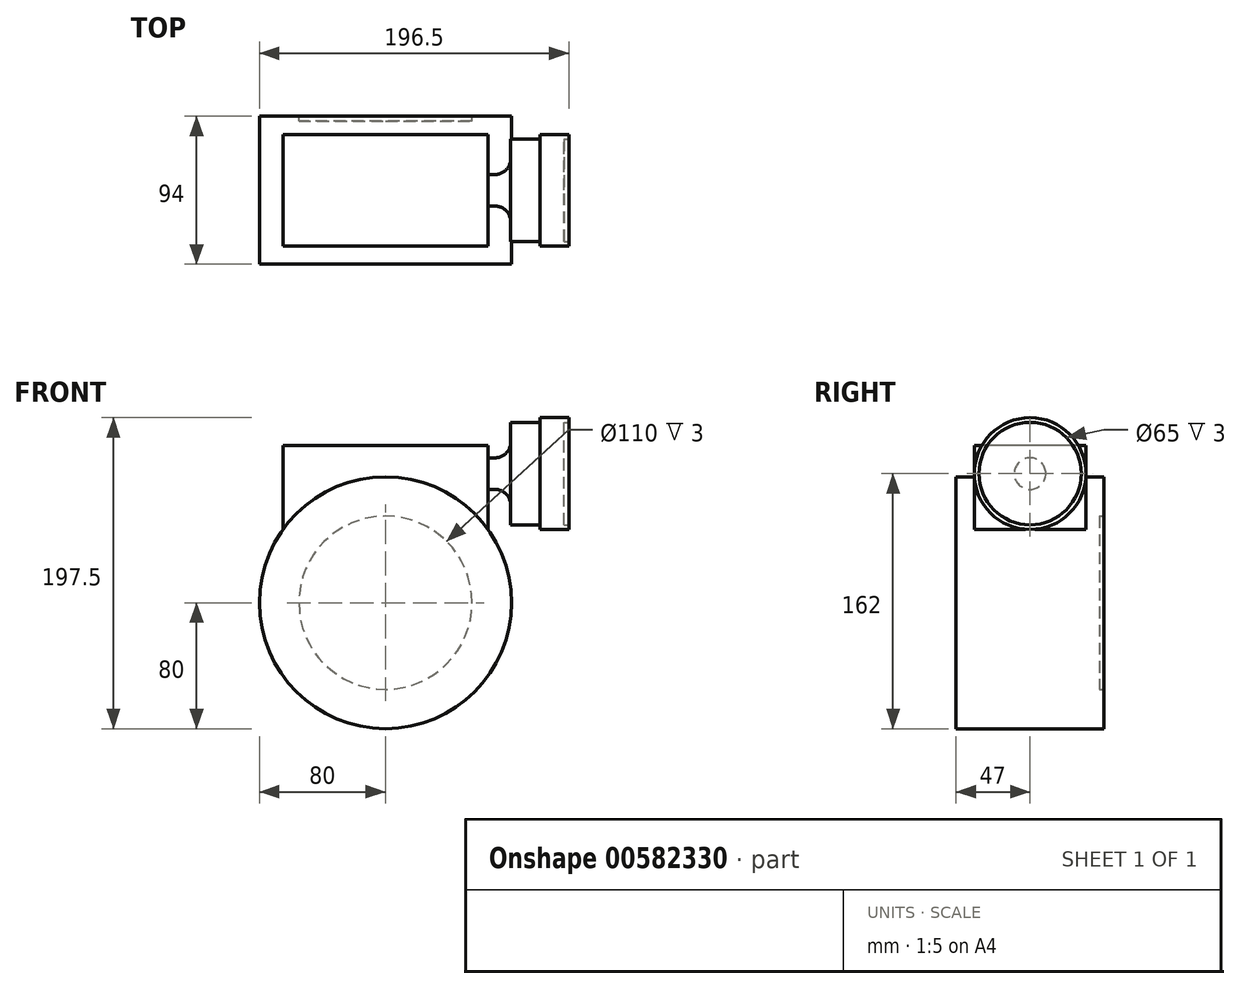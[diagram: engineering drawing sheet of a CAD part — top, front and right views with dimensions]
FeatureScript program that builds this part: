
annotation { "Feature Type Name" : "Feature", "Feature Type Description" : "" }
export const myFeature = defineFeature(function(context is Context, id is Id, definition is map)
    precondition{}
    {
        {
            var Q0;
            Q0=qCreatedBy(makeId("Front.planeOp"),FACE);
            var sketch = newSketch(context, id + "F0", { "sketchPlane" : qUnion([Q0])});
            skCircle(sketch, "E0", {"center": v(0, 0) * mm, "radius": 80 * mm});
            skSolve(sketch);
        }
        {
            var Q0;
            Q0=makeQuery(id+"F0.imprint","IMPRINT",FACE,{"disambiguationData":[TD([[makeQuery(id+"F0.imprint","IMPRINT",EDGE,{"derivedFrom":sQuery(id+"F0.wireOp",EDGE,"E0")}),1.0]])]});
            extrude(context, id + "F1", {"entities" : qUnion([Q0]), "depth" : 47 * mm, "offsetDistance" : 25 * mm});
        }
        {
            var Q0;
            Q0=qCreatedBy(makeId("Top.planeOp"),FACE);
            var sketch = newSketch(context, id + "F2", { "sketchPlane" : qUnion([Q0])});
            skLineSegment(sketch, "E1.bottom", {"start": v(-65, 35.5) * mm, "end": v(65, 35.5) * mm});
            skLineSegment(sketch, "E1.top", {"start": v(-65, -35.5) * mm, "end": v(65, -35.5) * mm});
            skLineSegment(sketch, "E1.left", {"start": v(-65, 35.5) * mm, "end": v(-65, -35.5) * mm});
            skLineSegment(sketch, "E1.right", {"start": v(65, 35.5) * mm, "end": v(65, -35.5) * mm});
            skPoint(sketch, "E1.middle", {"position": v(0, 0) * mm});
            skSolve(sketch);
        }
        {
            var Q0;
            Q0=makeQuery(id+"F2.imprint","IMPRINT",FACE,{"disambiguationData":[TD([[makeQuery(id+"F2.imprint","IMPRINT",EDGE,{"derivedFrom":sQuery(id+"F2.wireOp",EDGE,"E1.bottom")}),-1.0]])]});
            extrude(context, id + "F3", {"entities" : qUnion([Q0]), "operationType" : NewBodyOperationType.ADD, "depth" : 100 * mm, "offsetDistance" : 25 * mm});
        }
        {
            var Q0;
            Q0=qCreatedBy(makeId("Front.planeOp"),FACE);
            var sketch = newSketch(context, id + "F4", { "sketchPlane" : qUnion([Q0])});
            skLineSegment(sketch, "E2.bottom", {"start": v(0, 92) * mm, "end": v(79.5, 92) * mm});
            skLineSegment(sketch, "E2.top", {"start": v(0, 82) * mm, "end": v(79.5, 82) * mm});
            skLineSegment(sketch, "E2.left", {"start": v(0, 92) * mm, "end": v(0, 82) * mm});
            skLineSegment(sketch, "E2.right", {"start": v(79.5, 92) * mm, "end": v(79.5, 82) * mm});
            skPoint(sketch, "E2.middle", {"position": v(39.75, 87) * mm});
            skLineSegment(sketch, "E3", {"start": v(79.5, 92) * mm, "end": v(79.5, 114.5) * mm});
            skLineSegment(sketch, "E4", {"start": v(79.5, 114.5) * mm, "end": v(98, 114.5) * mm});
            skLineSegment(sketch, "E5", {"start": v(98, 114.5) * mm, "end": v(98, 117.5) * mm});
            skLineSegment(sketch, "E6", {"start": v(98, 117.5) * mm, "end": v(116.5, 117.5) * mm});
            skLineSegment(sketch, "E7", {"start": v(116.5, 117.5) * mm, "end": v(116.5, 114.5) * mm});
            skLineSegment(sketch, "E8", {"start": v(116.5, 114.5) * mm, "end": v(113.5, 114.5) * mm});
            skLineSegment(sketch, "E9", {"start": v(113.5, 114.5) * mm, "end": v(113.5, 82) * mm});
            skLineSegment(sketch, "E10", {"start": v(113.5, 82) * mm, "end": v(79.5, 82) * mm});
            skSolve(sketch);
        }
        {
            var Q0;
            Q0=makeQuery(id+"F4.imprint","IMPRINT",FACE,{"disambiguationData":[TD([[makeQuery(id+"F4.imprint","IMPRINT",EDGE,{"derivedFrom":sQuery(id+"F4.wireOp",EDGE,"E2.right")}),1.0]])]});
            var Q1;
            Q1=makeQuery(id+"F4.imprint","IMPRINT",FACE,{"disambiguationData":[TD([[makeQuery(id+"F4.imprint","IMPRINT",EDGE,{"derivedFrom":sQuery(id+"F4.wireOp",EDGE,"E2.bottom")}),-1.0]])]});
            var Q2;
            Q2=sQuery(id+"F4.wireOp",EDGE,"E10");
            revolve(context, id + "F5", {"operationType" : NewBodyOperationType.ADD, "entities" : qUnion([Q0, Q1]), "axis" : qUnion([Q2]), "revolveType" : RevolveType.FULL});
        }
        {
            var Q0;
            Q0=makeQuery(id+"F5.opRevolve","SWEPT_EDGE",EDGE,{"disambiguationData":[OSD([sQuery(id+"F4.wireOp",EDGE,"E2.bottom"),sQuery(id+"F4.wireOp",EDGE,"E2.right"),sQuery(id+"F4.wireOp",EDGE,"E3")])]});
            fillet(context, id + "F6", {"entities" : qUnion([Q0]), "radius" : 10 * mm, "tangentPropagation" : true, "allowEdgeOverflow" : false});
        }
        {
            var Q0;
            Q0=qCreatedBy(makeId("Front.planeOp"),FACE);
            var sketch = newSketch(context, id + "F7", { "sketchPlane" : qUnion([Q0])});
            skCircle(sketch, "E11", {"center": v(0, 0) * mm, "radius": 80 * mm});
            skSolve(sketch);
        }
        {
            var Q0;
            Q0=makeQuery(id+"F7.imprint","IMPRINT",FACE,{"disambiguationData":[TD([[makeQuery(id+"F7.imprint","IMPRINT",EDGE,{"derivedFrom":sQuery(id+"F7.wireOp",EDGE,"E11")}),1.0]])]});
            extrude(context, id + "F8", {"entities" : qUnion([Q0]), "operationType" : NewBodyOperationType.ADD, "oppositeDirection" : true, "depth" : (94 - 47) * mm, "offsetDistance" : 25 * mm});
        }
        {
            var Q0;
            Q0=makeQuery(id+"F8.opExtrude","CAP_FACE",FACE,{"disambiguationData":[OSD([sQuery(id+"F7.wireOp",EDGE,"E11")])],"isStart":false});
            var sketch = newSketch(context, id + "F9", { "sketchPlane" : qUnion([Q0])});
            skCircle(sketch, "E12", {"center": v(0, 0) * mm, "radius": 55 * mm});
            skSolve(sketch);
        }
        {
            var Q0;
            Q0=makeQuery(id+"F9.imprint","IMPRINT",FACE,{"disambiguationData":[TD([[makeQuery(id+"F9.imprint","IMPRINT",EDGE,{"derivedFrom":sQuery(id+"F9.wireOp",EDGE,"E12")}),1.0]])]});
            extrude(context, id + "F10", {"entities" : qUnion([Q0]), "operationType" : NewBodyOperationType.REMOVE, "oppositeDirection" : true, "depth" : 3 * mm, "offsetDistance" : 25 * mm});
        }
    });
